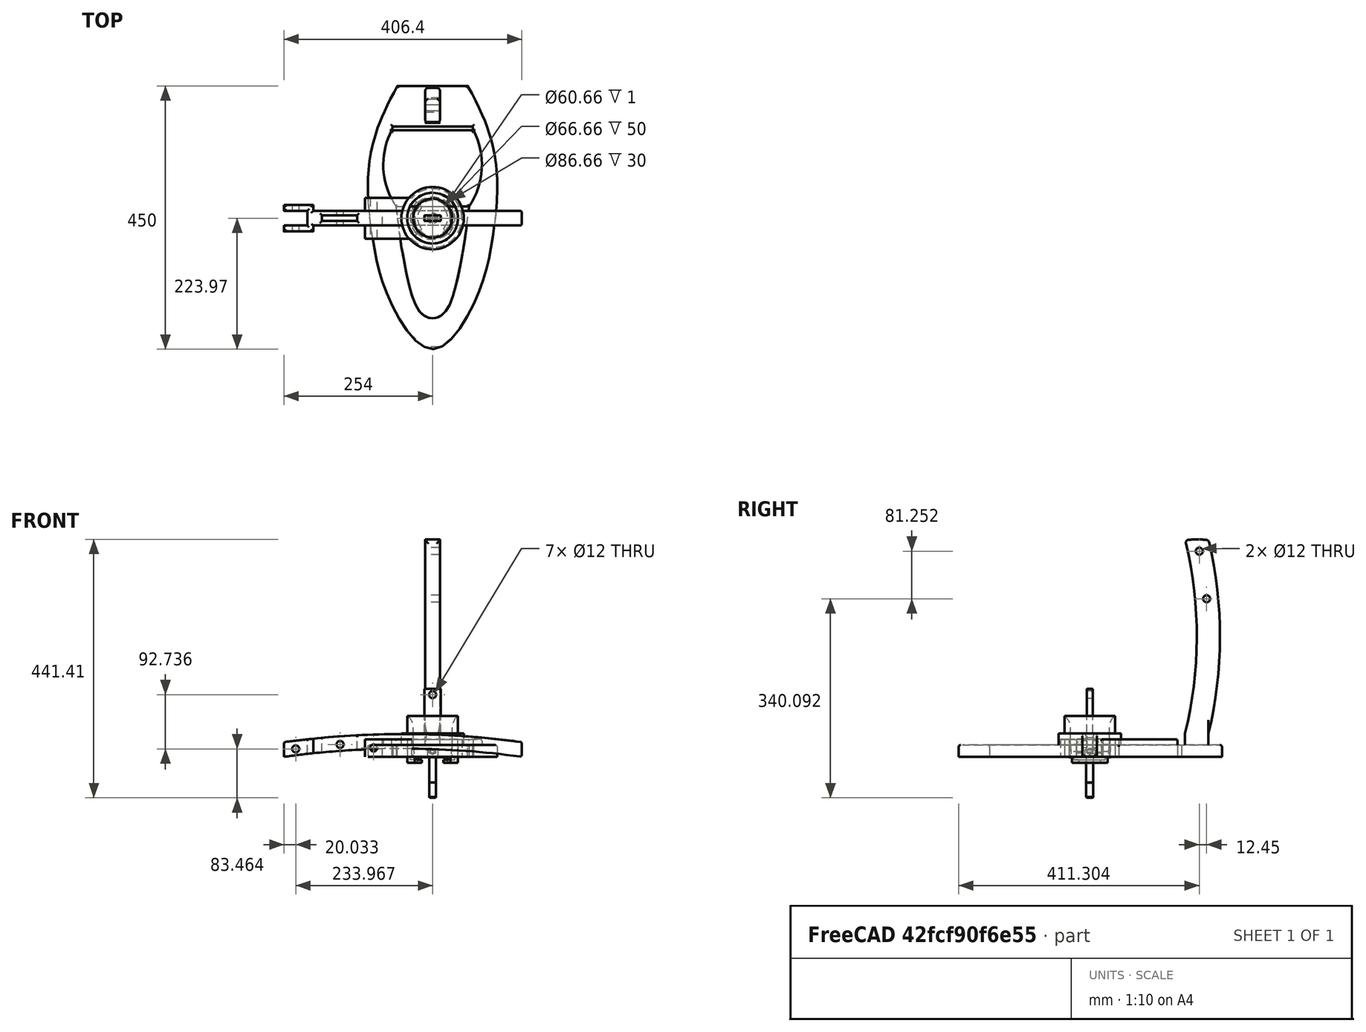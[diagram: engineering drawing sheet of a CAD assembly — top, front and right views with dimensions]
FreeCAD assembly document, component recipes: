
FREECAD ASSEMBLY — COMPONENT RECIPES ("Espresso Machine")

This assembly document has 8 components, labeled P0..P7 below (a component is one placed body or linked part). 5 of them carry a construction recipe — the FreeCAD feature program that regenerates the part from scratch, quoted from this document or its linked companion documents; the rest are supplied as boundary geometry only. No exploded tour is included for this assembly.
COMPONENT P0 — geometry summary ("M12x45-Screw002"; no construction recipe available for this part):
  bounding box: 57.0 x 18.0 x 18.0 mm
  tessellated surface: 6,456 triangles
  volume: 7653 mm^3 (41% of its bounding box)
  symmetry: 6-fold rotationally symmetric about the x axis
COMPONENT P1 — geometry summary ("M6x70-Screw001"; no construction recipe available for this part):
  bounding box: 82.0 x 18.0 x 18.0 mm
  tessellated surface: 6,456 triangles
  volume: 10481 mm^3 (39% of its bounding box)
  symmetry: 6-fold rotationally symmetric about the x axis
COMPONENT P2 — geometry summary ("M6x70-Screw002"; no construction recipe available for this part):
  bounding box: 82.0 x 18.0 x 18.0 mm
  tessellated surface: 6,456 triangles
  volume: 10481 mm^3 (39% of its bounding box)
  symmetry: 6-fold rotationally symmetric about the x axis
COMPONENT P3 — recipe-attached ("Plunger001", modeled in this document).
Construction recipe (the document's own serialized feature program — sketch geometry with constraints, then the solid features built on it; lengths are millimeters unless a unit is written):

FEATURE [Sketcher::SketchObject] Sketch016
  ArcFitTolerance = 1e-06
  AttachmentSupport = -> [YZ_Plane004]
  FullyConstrained = true
  MakeInternals = false
  MapMode = 5
  Placement = pos=(0,0,0) rot=(0.57735,0.57735,0.57735;2.0944rad)
  sketch-geometry (6):
    g0: LineSegment StartX=0 StartY=40 StartZ=0 EndX=33.33 EndY=40 EndZ=0
    g1: LineSegment StartX=33.33 StartY=40 StartZ=0 EndX=33.33 EndY=20 EndZ=0
    g2: LineSegment StartX=31.8 StartY=1.61e-14 StartZ=0 EndX=0 EndY=0 EndZ=0
    g3: ArcOfCircle CenterX=163.284 CenterY=1.61e-14 CenterZ=0 NormalX=0 NormalY=0 NormalZ=1 AngleXU=0 Radius=131.484 StartAngle=2.98889 EndAngle=3.14159
    g4: LineSegment StartX=0 StartY=40 StartZ=0 EndX=0 EndY=0 EndZ=0
    g5: LineSegment [constr] StartX=31.8 StartY=1.61e-14 StartZ=0 EndX=163.284 EndY=1.61e-14 EndZ=0
  constraints (17):
    c: PointOnObject(g0,g-2)
    c: Horizontal(g0)
    c: Coincident(g0,g1)
    c: Vertical(g1)
    c: PointOnObject(g2,g-1)
    c: Coincident(g2,g-1)
    c: Coincident(g3,g1)
    c: Coincident(g3,g2)
    c: DistanceX(g0,g0) = 33.33
    c: Coincident(g4,g0)
    c: Coincident(g4,g2)
    c: DistanceY(g4,g4) = 40
    c: DistanceY(g1,g1) = 20
    c: DistanceX(g2,g2) = 31.8
    c: Coincident(g5,g2)
    c: Coincident(g5,g3)
    c: Horizontal(g5)
FEATURE [PartDesign::Revolution] Revolution004
  Angle = 360
  Angle2 = 60
  Axis = (0,0,1)
  Base = (0,0,0)
  Placement = pos=(0,0,0) rot=(1,1,1;2.0944rad)
  Profile = -> Sketch016
  ReferenceAxis = -> Sketch016 [V_Axis]
  Refine = true
  Reversed = true
  Suppressed = false
  Type = 0
FEATURE [Sketcher::SketchObject] Sketch017
  ArcFitTolerance = 1e-06
  AttachmentSupport = -> [Revolution004]
  FullyConstrained = true
  MakeInternals = false
  MapMode = 5
  Placement = pos=(-8.8e-15,0,40) rot=(0,0,-1;1.5708rad)
  expr: Constraints[8] = VarSet.Plunger_Clearance_Length - 2.5 mm
  sketch-geometry (4):
    g0: LineSegment StartX=-4.995 StartY=13.75 StartZ=0 EndX=-4.995 EndY=-13.75 EndZ=0
    g1: LineSegment StartX=-4.995 StartY=-13.75 StartZ=0 EndX=4.995 EndY=-13.75 EndZ=0
    g2: LineSegment StartX=4.995 StartY=-13.75 StartZ=0 EndX=4.995 EndY=13.75 EndZ=0
    g3: LineSegment StartX=4.995 StartY=13.75 StartZ=0 EndX=-4.995 EndY=13.75 EndZ=0
  constraints (10):
    c: Coincident(g0,g1)
    c: Coincident(g1,g2)
    c: Coincident(g2,g3)
    c: Coincident(g3,g0)
    c: Vertical(g0)
    c: Horizontal(g1)
    c: Symmetric(g0,g2,g-2)
    c: Symmetric(g2,g1,g-1)
    c: DistanceY(g2,g2) = 27.5
    c: Distance(g3,g3) = 9.99
FEATURE [PartDesign::Pad] Pad007
  BaseFeature = -> Revolution004
  Direction = (0,0,1)
  Length = 76.2
  Length2 = 10
  Placement = pos=(0,0,0) rot=(1,1,1;2.0944rad)
  Profile = -> Sketch017
  ReferenceAxis = -> Sketch017 [N_Axis]
  Refine = true
  Suppressed = false
  Type = 0
FEATURE [Sketcher::SketchObject] Sketch018
  ArcFitTolerance = 1e-06
  AttachmentSupport = -> [Pad007]
  ExternalGeometry = -> [Pad007]
  FullyConstrained = true
  MakeInternals = false
  MapMode = 5
  Placement = pos=(0,-4.995,0) rot=(0.57735,0.57735,-0.57735;2.0944rad)
  sketch-geometry (1):
    g0: Circle CenterX=-106.2 CenterY=0 CenterZ=0 NormalX=0 NormalY=0 NormalZ=1 AngleXU=0 Radius=6
  constraints (3):
    c: PointOnObject(g0,g-1)
    c: Diameter(g0) = 12
    c: Distance(g0,g-3) = 10
FEATURE [PartDesign::Pocket] Pocket005
  BaseFeature = -> Pad007
  Direction = (0,1,0)
  Length = 5
  Length2 = 5
  Placement = pos=(0,0,0) rot=(1,1,1;2.0944rad)
  Profile = -> Sketch018
  ReferenceAxis = -> Sketch018 [N_Axis]
  Refine = true
  Suppressed = false
  Type = 1
FEATURE [PartDesign::Fillet] Fillet003
  Base = -> Pocket005 [Face8,Edge15,Edge8,Edge10,Edge12]
  BaseFeature = -> Pocket005
  Placement = pos=(0,0,0) rot=(1,1,1;2.0944rad)
  Radius = 1
  Refine = true
  SupportTransform = false
  Suppressed = false
  UseAllEdges = false
FEATURE [PartDesign::Fillet] Fillet004
  Base = -> Fillet003 [Edge28,Edge47]
  BaseFeature = -> Fillet003
  Placement = pos=(0,0,0) rot=(1,1,1;2.0944rad)
  Radius = 1
  Refine = true
  SupportTransform = false
  Suppressed = false
  UseAllEdges = false
FEATURE [PartDesign::Body] Body004  label="Plunger"
  AllowCompound = false
  Group = -> [Sketch016,Revolution004,Sketch017,Pad007,Sketch018,Pocket005,Fillet003,Fillet004]
  Origin = -> Origin004
  Tip = -> Fillet004
COMPONENT P4 — recipe-attached ("Pressure Vessel001", modeled in this document).
Construction recipe (the document's own serialized feature program — sketch geometry with constraints, then the solid features built on it; lengths are millimeters unless a unit is written):

FEATURE [Sketcher::SketchObject] Sketch
  ArcFitTolerance = 1e-06
  AttachmentSupport = -> [XY_Plane]
  FullyConstrained = true
  MakeInternals = false
  MapMode = 5
  sketch-geometry (2):
    g0: Circle CenterX=0 CenterY=0 CenterZ=0 NormalX=0 NormalY=0 NormalZ=1 AngleXU=0 Radius=33.33
    g1: Circle CenterX=0 CenterY=0 CenterZ=0 NormalX=0 NormalY=0 NormalZ=1 AngleXU=0 Radius=43.33
  constraints (4):
    c: Coincident(g0,g-1)
    c: Coincident(g1,g0)
    c: Diameter(g0) = 66.66
    c: Diameter(g1) = 86.66
FEATURE [PartDesign::Pad] Pad
  Direction = (0,0,1)
  Length = 50
  Length2 = 10
  Profile = -> Sketch
  ReferenceAxis = -> Sketch [N_Axis]
  Refine = true
  Suppressed = false
  Type = 0
FEATURE [Sketcher::SketchObject] Sketch001
  ArcFitTolerance = 1e-06
  AttachmentSupport = -> [XZ_Plane]
  ExternalGeometry = -> [Pad]
  FullyConstrained = true
  MakeInternals = false
  MapMode = 5
  Placement = pos=(0,0,0) rot=(1,0,0;1.5708rad)
  sketch-geometry (4):
    g0: LineSegment StartX=33.33 StartY=50 StartZ=0 EndX=43.33 EndY=50 EndZ=0
    g1: LineSegment StartX=43.33 StartY=50 StartZ=0 EndX=43.33 EndY=70 EndZ=0
    g2: ArcOfCircle CenterX=58.33 CenterY=50 CenterZ=0 NormalX=0 NormalY=0 NormalZ=1 AngleXU=0 Radius=25 StartAngle=2.2143 EndAngle=3.14159
    g3: LineSegment [constr] StartX=33.33 StartY=50 StartZ=0 EndX=33.33 EndY=0 EndZ=0
  constraints (11):
    c: Coincident(g0,g-4)
    c: Coincident(g0,g-3)
    c: Coincident(g0,g1)
    c: Vertical(g1)
    c: DistanceY(g1,g1) = 20
    c: Coincident(g2,g0)
    c: Coincident(g2,g1)
    c: Coincident(g3,g0)
    c: PointOnObject(g3,g-1)
    c: Vertical(g3)
    c: Tangent(g3,g2)
FEATURE [PartDesign::Revolution] Revolution
  Angle = 360
  Angle2 = 60
  Axis = (0,2e-16,1)
  Base = (0,0,0)
  BaseFeature = -> Pad
  Profile = -> Sketch001
  ReferenceAxis = -> Sketch001 [V_Axis]
  Refine = true
  Suppressed = false
  Type = 0
FEATURE [Sketcher::SketchObject] Sketch002
  ArcFitTolerance = 1e-06
  AttachmentSupport = -> [XZ_Plane]
  ExternalGeometry = -> [Revolution]
  FullyConstrained = true
  MakeInternals = false
  MapMode = 5
  Placement = pos=(0,0,0) rot=(1,0,0;1.5708rad)
  sketch-geometry (8):
    g0: LineSegment StartX=43.33 StartY=0 StartZ=0 EndX=43.33 EndY=-10 EndZ=0
    g1: LineSegment StartX=43.33 StartY=-10 StartZ=0 EndX=25.83 EndY=-10 EndZ=0
    g2: LineSegment StartX=25.83 StartY=-10 StartZ=0 EndX=25.83 EndY=-5 EndZ=0
    g3: LineSegment StartX=25.83 StartY=-5 StartZ=0 EndX=38.33 EndY=-5 EndZ=0
    g4: LineSegment StartX=38.33 StartY=-5 StartZ=0 EndX=38.33 EndY=0 EndZ=0
    g5: LineSegment [constr] StartX=43.33 StartY=0 StartZ=0 EndX=38.33 EndY=0 EndZ=0
    g6: LineSegment [constr] StartX=38.33 StartY=0 StartZ=0 EndX=33.33 EndY=0 EndZ=0
    g7: LineSegment StartX=38.33 StartY=0 StartZ=0 EndX=43.33 EndY=0 EndZ=0
  constraints (21):
    c: Coincident(g0,g-3)
    c: Vertical(g0)
    c: Coincident(g0,g1)
    c: Horizontal(g1)
    c: Coincident(g1,g2)
    c: Vertical(g2)
    c: Coincident(g2,g3)
    c: Coincident(g4,g3)
    c: PointOnObject(g4,g-1)
    c: Vertical(g4)
    c: Horizontal(g3)
    c: DistanceX(g1,g1) = 17.5
    c: DistanceY(g0,g0) = 10
    c: Equal(g2,g4)
    c: Coincident(g5,g0)
    c: Coincident(g5,g4)
    c: Coincident(g6,g4)
    c: Coincident(g6,g-4)
    c: Equal(g6,g5)
    c: Coincident(g7,g4)
    c: Coincident(g7,g0)
FEATURE [PartDesign::Revolution] Revolution001
  Angle = 90
  Angle2 = 60
  Axis = (0,2e-16,1)
  Base = (0,0,0)
  BaseFeature = -> Revolution
  Midplane = true
  Profile = -> Sketch002
  ReferenceAxis = -> Sketch002 [V_Axis]
  Refine = true
  Suppressed = false
  Type = 0
FEATURE [PartDesign::Mirrored] Mirrored
  BaseFeature = -> Revolution001
  MirrorPlane = -> Sketch002 [V_Axis]
  Originals = -> [Revolution001]
  Refine = true
  Suppressed = false
  TransformMode = 0
FEATURE [Sketcher::SketchObject] Sketch003
  ArcFitTolerance = 1e-06
  AttachmentSupport = -> [XZ_Plane]
  ExternalGeometry = -> [Mirrored]
  FullyConstrained = true
  MakeInternals = false
  MapMode = 5
  Placement = pos=(0,0,0) rot=(1,0,0;1.5708rad)
  sketch-geometry (5):
    g0: LineSegment StartX=36.33 StartY=0 StartZ=0 EndX=33.33 EndY=0 EndZ=0
    g1: LineSegment StartX=33.33 StartY=0 StartZ=0 EndX=30.33 EndY=0 EndZ=0
    g2: LineSegment StartX=30.33 StartY=0 StartZ=0 EndX=30.33 EndY=-1 EndZ=0
    g3: LineSegment StartX=30.33 StartY=-1 StartZ=0 EndX=36.33 EndY=-1 EndZ=0
    g4: LineSegment StartX=36.33 StartY=-1 StartZ=0 EndX=36.33 EndY=0 EndZ=0
  constraints (14):
    c: PointOnObject(g0,g-1)
    c: Coincident(g0,g-3)
    c: Coincident(g0,g1)
    c: Horizontal(g1)
    c: Coincident(g1,g2)
    c: Vertical(g2)
    c: Coincident(g2,g3)
    c: Horizontal(g3)
    c: Coincident(g3,g4)
    c: Coincident(g4,g0)
    c: Vertical(g4)
    c: Equal(g1,g0)
    c: DistanceX(g3,g3) = 6
    c: DistanceY(g4,g4) = 1
FEATURE [PartDesign::Revolution] Revolution002
  Angle = 360
  Angle2 = 60
  Axis = (0,2e-16,1)
  Base = (0,0,0)
  BaseFeature = -> Mirrored
  Midplane = true
  Profile = -> Sketch003
  ReferenceAxis = -> Sketch003 [V_Axis]
  Refine = true
  Suppressed = false
  Type = 0
FEATURE [Sketcher::SketchObject] Sketch004
  ArcFitTolerance = 1e-06
  AttachmentSupport = -> [XZ_Plane]
  ExternalGeometry = -> [Revolution002]
  FullyConstrained = true
  MakeInternals = false
  MapMode = 5
  Placement = pos=(0,0,0) rot=(1,0,0;1.5708rad)
  sketch-geometry (4):
    g0: LineSegment StartX=33.33 StartY=20 StartZ=0 EndX=53.33 EndY=20 EndZ=0
    g1: LineSegment StartX=53.33 StartY=20 StartZ=0 EndX=53.33 EndY=40 EndZ=0
    g2: LineSegment StartX=53.33 StartY=40 StartZ=0 EndX=33.33 EndY=40 EndZ=0
    g3: LineSegment StartX=33.33 StartY=40 StartZ=0 EndX=33.33 EndY=20 EndZ=0
  constraints (12):
    c: Horizontal(g0)
    c: Horizontal(g2)
    c: Vertical(g1)
    c: Vertical(g3)
    c: DistanceX(g2,g2) = 20
    c: DistanceY(g1,g1) = 20
    c: Coincident(g1,g0)
    c: Coincident(g2,g1)
    c: Coincident(g3,g2)
    c: Coincident(g3,g0)
    c: PointOnObject(g0,g-3)
    c: DistanceY(g-1,g0) = 20
FEATURE [PartDesign::Revolution] Revolution003
  Angle = 360
  Angle2 = 60
  Axis = (0,2e-16,1)
  Base = (0,0,0)
  BaseFeature = -> Revolution002
  Profile = -> Sketch004
  ReferenceAxis = -> Sketch004 [V_Axis]
  Refine = true
  Suppressed = false
  Type = 0
FEATURE [PartDesign::Body] Body  label="Pressure Vessel"
  AllowCompound = false
  Group = -> [Sketch,Pad,Sketch001,Revolution,Sketch002,Revolution001,Mirrored,Sketch003,Revolution002,Sketch004,Revolution003]
  Origin = -> Origin
  Tip = -> Revolution003
COMPONENT P5 — recipe-attached ("Presure Lever001", modeled in this document).
Construction recipe (the document's own serialized feature program — sketch geometry with constraints, then the solid features built on it; lengths are millimeters unless a unit is written):

FEATURE [Sketcher::SketchObject] Sketch011
  ArcFitTolerance = 1e-06
  AttachmentSupport = -> [XY_Plane002]
  FullyConstrained = true
  MakeInternals = false
  MapMode = 5
  expr: Constraints[43] = VarSet.Plunger_Clearance_Length * 2
  expr: Constraints[45] = VarSet.Plunger_Clearance_Length / 2
  sketch-geometry (16):
    g0: LineSegment StartX=-214 StartY=-12.5 StartZ=0 EndX=-214 EndY=12.5 EndZ=0
    g1: LineSegment StartX=-214 StartY=12.5 StartZ=0 EndX=-254 EndY=12.5 EndZ=0
    g2: LineSegment StartX=-254 StartY=12.5 StartZ=0 EndX=-254 EndY=22.5 EndZ=0
    g3: LineSegment StartX=152.4 StartY=12.5 StartZ=0 EndX=152.4 EndY=-12.5 EndZ=0
    g4: LineSegment StartX=-254 StartY=-22.5 StartZ=0 EndX=-254 EndY=-12.5 EndZ=0
    g5: LineSegment StartX=-254 StartY=-12.5 StartZ=0 EndX=-214 EndY=-12.5 EndZ=0
    g6: LineSegment StartX=-254 StartY=22.5 StartZ=0 EndX=-204 EndY=22.5 EndZ=0
    g7: LineSegment StartX=-204 StartY=22.5 StartZ=0 EndX=-204 EndY=12.5 EndZ=0
    g8: LineSegment StartX=-204 StartY=12.5 StartZ=0 EndX=152.4 EndY=12.5 EndZ=0
    g9: LineSegment StartX=-254 StartY=-22.5 StartZ=0 EndX=-204 EndY=-22.5 EndZ=0
    g10: LineSegment StartX=-204 StartY=-22.5 StartZ=0 EndX=-204 EndY=-12.5 EndZ=0
    g11: LineSegment StartX=-204 StartY=-12.5 StartZ=0 EndX=152.4 EndY=-12.5 EndZ=0
    g12: LineSegment StartX=-189 StartY=5 StartZ=0 EndX=-189 EndY=-5 EndZ=0
    g13: LineSegment StartX=-189 StartY=-5 StartZ=0 EndX=-129 EndY=-5 EndZ=0
    g14: LineSegment StartX=-129 StartY=-5 StartZ=0 EndX=-129 EndY=5 EndZ=0
    g15: LineSegment StartX=-129 StartY=5 StartZ=0 EndX=-189 EndY=5 EndZ=0
  constraints (46):
    c: Coincident(g0,g1)
    c: Horizontal(g1)
    c: Coincident(g1,g2)
    c: Vertical(g2)
    c: Vertical(g4)
    c: Coincident(g4,g5)
    c: Coincident(g5,g0)
    c: Horizontal(g5)
    c: Equal(g2,g4)
    c: Symmetric(g3,g3,g-1)
    c: DistanceY(g0,g0) = 25
    c: DistanceX(g1,g1) = 40
    c: Equal(g1,g5)
    c: Symmetric(g0,g0,g-1)
    c: DistanceY(g2,g2) = 10
    c: Coincident(g2,g6)
    c: Horizontal(g6)
    c: Coincident(g6,g7)
    c: Vertical(g7)
    c: Coincident(g7,g8)
    c: Horizontal(g8)
    c: Coincident(g4,g9)
    c: Horizontal(g9)
    c: Coincident(g9,g10)
    c: Vertical(g10)
    c: Coincident(g10,g11)
    c: Horizontal(g11)
    c: Vertical(g11,g8)
    c: Vertical(g7,g10)
    c: Equal(g7,g10)
    c: Horizontal(g0,g7)
    c: DistanceX(g0,g7) = 10
    c: DistanceX(g2,g3) = 406.4
    c: Coincident(g8,g3)
    c: Distance(g3,g-2) = 152.4
    c: Coincident(g12,g13)
    c: Coincident(g13,g14)
    c: Coincident(g14,g15)
    c: Coincident(g15,g12)
    c: Vertical(g12)
    c: Horizontal(g13)
    c: Horizontal(g15)
    c: Symmetric(g14,g13,g-1)
    c: DistanceX(g15,g15) = 60
    c: Distance(g14,g14) = 10
    c: DistanceX(g7,g12) = 15
FEATURE [PartDesign::Pad] Pad005
  Direction = (0,0,1)
  Length = 40
  Length2 = 10
  Profile = -> Sketch011
  ReferenceAxis = -> Sketch011 [N_Axis]
  Refine = true
  Suppressed = false
  Type = 0
FEATURE [Sketcher::SketchObject] Sketch012
  ArcFitTolerance = 1e-06
  AttachmentSupport = -> [Pad005]
  ExternalGeometry = -> [Pad005]
  FullyConstrained = true
  MakeInternals = false
  MapMode = 5
  Placement = pos=(0,-12.5,0) rot=(1,0,0;1.5708rad)
  sketch-geometry (6):
    g0: ArcOfCircle CenterX=-50.8 CenterY=-1468.03 CenterZ=0 NormalX=0 NormalY=0 NormalZ=1 AngleXU=0 Radius=1482.03 StartAngle=1.43325 EndAngle=1.70834
    g1: ArcOfCircle CenterX=-50.8 CenterY=-1468.03 CenterZ=0 NormalX=0 NormalY=0 NormalZ=1 AngleXU=0 Radius=1506.8 StartAngle=1.43553 EndAngle=1.70606
    g2: LineSegment StartX=-254 StartY=2.274e-13 StartZ=0 EndX=152.4 EndY=-2.274e-13 EndZ=0
    g3: LineSegment StartX=-254 StartY=25 StartZ=0 EndX=-254 EndY=40 EndZ=0
    g4: LineSegment StartX=152.4 StartY=40 StartZ=0 EndX=152.4 EndY=25 EndZ=0
    g5: LineSegment StartX=-254 StartY=40 StartZ=0 EndX=152.4 EndY=40 EndZ=0
  constraints (15):
    c: Coincident(g0,g-5)
    c: Coincident(g0,g-6)
    c: PointOnObject(g1,g-5)
    c: PointOnObject(g1,g-6)
    c: Coincident(g1,g0)
    c: DistanceY(g0,g1) = 25
    c: Coincident(g2,g0)
    c: Coincident(g2,g0)
    c: Coincident(g3,g1)
    c: Coincident(g3,g-9)
    c: Coincident(g4,g-8)
    c: Coincident(g4,g1)
    c: Coincident(g5,g3)
    c: Coincident(g5,g4)
    c: Radius(g0) = 1482.03
FEATURE [PartDesign::Pocket] Pocket002
  BaseFeature = -> Pad005
  Direction = (0,1,-2e-16)
  Length = 5
  Length2 = 5
  Midplane = true
  Profile = -> Sketch012
  ReferenceAxis = -> Sketch012 [N_Axis]
  Refine = true
  Suppressed = false
  Type = 1
FEATURE [PartDesign::Fillet] Fillet002
  Base = -> Pocket002 [Face14,Face4]
  BaseFeature = -> Pocket002
  Radius = 3
  Refine = true
  SupportTransform = false
  Suppressed = false
  UseAllEdges = false
FEATURE [Sketcher::SketchObject] Sketch013
  ArcFitTolerance = 1e-06
  AttachmentSupport = -> [Fillet002]
  ExternalGeometry = -> [Fillet002]
  FullyConstrained = true
  MakeInternals = false
  MapMode = 5
  Placement = pos=(0,-12.5,0) rot=(1,0,0;1.5708rad)
  sketch-geometry (6):
    g0: Circle CenterX=-158.2 CenterY=21.0121 CenterZ=0 NormalX=0 NormalY=0 NormalZ=1 AngleXU=0 Radius=6
    g1: Circle CenterX=-233.967 CenterY=13.4636 CenterZ=0 NormalX=0 NormalY=0 NormalZ=1 AngleXU=0 Radius=6
    g2: LineSegment [constr] StartX=-159.034 StartY=31.8641 StartZ=0 EndX=-158.2 EndY=21.0121 EndZ=0
    g3: LineSegment [constr] StartX=-158.2 StartY=21.0121 StartZ=0 EndX=-157.366 EndY=10.1601 EndZ=0
    g4: LineSegment [constr] StartX=-254 StartY=21.9723 StartZ=0 EndX=-214 EndY=4.98325 EndZ=0
    g5: LineSegment [constr] StartX=-214 StartY=26.8823 StartZ=0 EndX=-254 EndY=2.238e-13 EndZ=0
  constraints (15):
    c: Diameter(g0) = 12
    c: Diameter(g1) = 12
    c: Symmetric(g-9,g-8,g2)
    c: Coincident(g0,g2)
    c: Coincident(g0,g3)
    c: Parallel(g3,g2)
    c: Equal(g2,g3)
    c: Coincident(g4,g-4)
    c: Coincident(g4,g-11)
    c: Coincident(g5,g-5)
    c: Coincident(g5,g-11)
    c: PointOnObject(g1,g4)
    c: PointOnObject(g1,g5)
    c: PointOnObject(g2,g-8)
    c: PointOnObject(g3,g-7)
FEATURE [PartDesign::Pocket] Pocket003
  BaseFeature = -> Fillet002
  Direction = (0,1,-2e-16)
  Length = 5
  Length2 = 5
  Midplane = true
  Profile = -> Sketch013
  ReferenceAxis = -> Sketch013 [N_Axis]
  Refine = true
  Suppressed = false
  Type = 1
FEATURE [PartDesign::Body] Body002  label="Presure Lever"
  AllowCompound = false
  Group = -> [Sketch011,Pad005,Sketch012,Pocket002,Fillet002,Sketch013,Pocket003]
  Origin = -> Origin002
  Tip = -> Pocket003
COMPONENT P6 — recipe-attached ("Stand001", modeled in this document).
Construction recipe (the document's own serialized feature program — sketch geometry with constraints, then the solid features built on it; lengths are millimeters unless a unit is written):

FEATURE [Sketcher::SketchObject] Sketch005
  ArcFitTolerance = 1e-06
  AttachmentSupport = -> [XY_Plane001]
  FullyConstrained = true
  MakeInternals = false
  MapMode = 5
  sketch-geometry (22):
    g0: LineSegment StartX=-60 StartY=226.026 StartZ=0 EndX=60 EndY=226.026 EndZ=0
    g1-g11: Circle [constr] x11 (B-spline internal-alignment scaffolding for g12; pole/knot coordinates omitted)
    g12: BSplineCurve PolesCount=11 KnotsCount=9 Degree=3 IsPeriodic=0
    g13-g21: GeomPoint [constr] x9 (B-spline internal-alignment scaffolding for g12; pole/knot coordinates omitted)
  constraints (15):
    c: Weight(g1) = 1
    c: Equal(g1, g2-g11) x10
    c: InternalAlignment(g1-g11 -> g12) x11
    c: InternalAlignment(g13-g21 -> g12) x9
    c: Coincident(g1,g0)
    c: PointOnObject(g6,g-2)
    c: Coincident(g11,g0)
    c: Symmetric(g19,g15,g-2)
    c: Symmetric(g18,g16,g-2)
    c: Symmetric(g20,g14,g-2)
    c: Symmetric(g10,g2,g-2)
    c: Distance(g17,g0) = 450
    c: Symmetric(g12,g12,g-2)
    c: DistanceX(g0,g0) = 120
    c: Block(g12)
FEATURE [PartDesign::Pad] Pad001
  Direction = (0,0,1)
  Length = 20
  Length2 = 10
  Profile = -> Sketch005
  ReferenceAxis = -> Sketch005 [N_Axis]
  Refine = true
  Suppressed = false
  Type = 0
FEATURE [Sketcher::SketchObject] Sketch006
  ArcFitTolerance = 1e-06
  AttachmentSupport = -> [Pad001]
  ExternalGeometry = -> [Pad001]
  FullyConstrained = true
  MakeInternals = false
  MapMode = 5
  Placement = pos=(0,0,20) rot=(0,0,1;0rad)
  sketch-geometry (8):
    g0: LineSegment StartX=-70 StartY=150 StartZ=0 EndX=70 EndY=150 EndZ=0
    g1: LineSegment StartX=-62.5 StartY=20 StartZ=0 EndX=62.5 EndY=20 EndZ=0
    g2: ArcOfCircle CenterX=42.9677 CenterY=91.301 CenterZ=0 NormalX=0 NormalY=0 NormalZ=1 AngleXU=0 Radius=127.308 StartAngle=2.66238 EndAngle=3.73606
    g3: LineSegment [constr] StartX=-109.336 StartY=82.5143 StartZ=0 EndX=-84.1287 EndY=83.9685 EndZ=0
    g4: ArcOfCircle CenterX=-42.9677 CenterY=91.301 CenterZ=0 NormalX=0 NormalY=0 NormalZ=1 AngleXU=0 Radius=127.308 StartAngle=5.68872 EndAngle=6.7624
    g5: LineSegment [constr] StartX=84.1287 StartY=83.9685 StartZ=0 EndX=109.336 EndY=82.5143 EndZ=0
    g6: LineSegment [constr] StartX=70 StartY=150 StartZ=0 EndX=95.2493 EndY=150 EndZ=0
    g7: LineSegment [constr] StartX=-70 StartY=150 StartZ=0 EndX=-95.2493 EndY=150 EndZ=0
  constraints (24):
    c: Symmetric(g0,g0,g-2)
    c: Symmetric(g1,g1,g-2)
    c: DistanceX(g0,g0) = 140
    c: DistanceX(g1,g1) = 125
    c: Distance(g-1,g0) = 150
    c: Coincident(g2,g0)
    c: Coincident(g2,g1)
    c: PointOnObject(g3,g-4)
    c: PointOnObject(g3,g2)
    c: Coincident(g4,g0)
    c: Coincident(g4,g1)
    c: PointOnObject(g5,g4)
    c: PointOnObject(g5,g-4)
    c: Symmetric(g0,g1,g5)
    c: Symmetric(g0,g1,g3)
    c: Equal(g3,g5)
    c: Coincident(g6,g0)
    c: PointOnObject(g6,g-4)
    c: Parallel(g6,g0)
    c: Equal(g6,g5)
    c: Coincident(g7,g0)
    c: PointOnObject(g7,g-4)
    c: Horizontal(g7)
    c: Distance(g-1,g1) = 20
FEATURE [PartDesign::Pad] Pad002
  BaseFeature = -> Pad001
  Direction = (0,0,1)
  Length = 10
  Length2 = 10
  Profile = -> Sketch006
  ReferenceAxis = -> Sketch006 [N_Axis]
  Refine = true
  Suppressed = false
  Type = 0
FEATURE [Sketcher::SketchObject] Sketch007
  ArcFitTolerance = 1e-06
  AttachmentSupport = -> [Pad002]
  ExternalGeometry = -> [Pad002]
  FullyConstrained = true
  MakeInternals = false
  MapMode = 5
  Placement = pos=(0,0,20) rot=(0,0,1;0rad)
  sketch-geometry (37):
    g0-g8: Circle [constr] x9 (B-spline internal-alignment scaffolding for g9; pole/knot coordinates omitted)
    g9: BSplineCurve PolesCount=9 KnotsCount=7 Degree=3 IsPeriodic=0
    g10-g16: GeomPoint [constr] x7 (B-spline internal-alignment scaffolding for g9; pole/knot coordinates omitted)
    g17: LineSegment [constr] StartX=-62.5 StartY=20 StartZ=0 EndX=-109.196 EndY=20 EndZ=0
    g18: LineSegment [constr] StartX=62.5 StartY=20 StartZ=0 EndX=109.196 EndY=20 EndZ=0
    g19: LineSegment [constr] StartX=54.2197 StartY=-43.9087 StartZ=0 EndX=100.915 EndY=-43.9087 EndZ=0
    g20: LineSegment [constr] StartX=-54.2197 StartY=-43.9087 StartZ=0 EndX=-100.915 EndY=-43.9087 EndZ=0
    g21: LineSegment [constr] StartX=49.9941 StartY=-66.9467 StartZ=0 EndX=96.6898 EndY=-66.9467 EndZ=0
    g22: LineSegment [constr] StartX=-49.9941 StartY=-66.9467 StartZ=0 EndX=-96.6898 EndY=-66.9467 EndZ=0
    g23: LineSegment [constr] StartX=-33.1368 StartY=-158.556 StartZ=0 EndX=-33.1368 EndY=-205.252 EndZ=0
    g24: LineSegment [constr] StartX=33.1368 StartY=-158.556 StartZ=0 EndX=33.1368 EndY=-205.252 EndZ=0
    g25: LineSegment [constr] StartX=0 StartY=-177.278 StartZ=0 EndX=0 EndY=-223.974 EndZ=0
    g26: LineSegment StartX=-62.5 StartY=20 StartZ=0 EndX=62.5 EndY=20 EndZ=0
    g27: LineSegment StartX=-70 StartY=150 StartZ=0 EndX=70 EndY=150 EndZ=0
    g28: LineSegment StartX=-70 StartY=150 StartZ=0 EndX=-68.2 EndY=156.718 EndZ=0
    g29: LineSegment StartX=70 StartY=150 StartZ=0 EndX=68.2 EndY=156.718 EndZ=0
    g30: LineSegment StartX=-68.2 StartY=156.718 StartZ=0 EndX=68.2 EndY=156.718 EndZ=0
    g31: LineSegment [constr] StartX=-109.196 StartY=20 StartZ=0 EndX=-100.915 EndY=-43.9087 EndZ=0
    g32: LineSegment [constr] StartX=-100.915 StartY=-43.9087 StartZ=0 EndX=-96.6898 EndY=-66.9467 EndZ=0
    g33: LineSegment [constr] StartX=109.196 StartY=20 StartZ=0 EndX=100.915 EndY=-43.9087 EndZ=0
    g34: LineSegment [constr] StartX=100.915 StartY=-43.9087 StartZ=0 EndX=96.6898 EndY=-66.9467 EndZ=0
    g35: LineSegment [constr] StartX=33.1368 StartY=-205.252 StartZ=0 EndX=0 EndY=-223.974 EndZ=0
    g36: LineSegment [constr] StartX=-33.1368 StartY=-205.252 StartZ=0 EndX=0 EndY=-223.974 EndZ=0
  constraints (66):
    c: Weight(g0) = 1
    c: Equal(g0, g1-g8) x8
    c: InternalAlignment(g0-g8 -> g9) x9
    c: InternalAlignment(g10-g16 -> g9) x7
    c: Coincident(g0,g-5)
    c: PointOnObject(g4,g-2)
    c: Coincident(g8,g-4)
    c: Symmetric(g11,g15,g-2)
    c: Symmetric(g12,g14,g-2)
    c: Symmetric(g7,g1,g-2)
    c: Coincident(g17,g9)
    c: PointOnObject(g17,g-6)
    c: Horizontal(g17)
    c: Coincident(g18,g9)
    c: PointOnObject(g18,g-6)
    c: Coincident(g19,g7)
    c: PointOnObject(g19,g-6)
    c: Coincident(g20,g1)
    c: PointOnObject(g20,g-6)
    c: Coincident(g21,g15)
    c: PointOnObject(g21,g-6)
    c: Coincident(g22,g11)
    c: PointOnObject(g22,g-6)
    c: Coincident(g23,g3)
    c: PointOnObject(g23,g-6)
    c: Coincident(g24,g5)
    c: PointOnObject(g24,g-6)
    c: Coincident(g25,g4)
    c: PointOnObject(g25,g-6)
    c: Vertical(g25)
    c: Equal(g23,g22)
    c: Equal(g22,g20)
    c: Equal(g20,g17)
    c: Equal(g18,g19)
    c: Equal(g19,g21)
    c: Equal(g21,g24)
    c: Equal(g23,g25)
    c: Equal(g24,g25)
    c: Parallel(g24,g23)
    c: Parallel(g22,g21)
    c: Coincident(g27,g-7)
    c: Coincident(g27,g-7)
    c: Coincident(g28,g27)
    c: Coincident(g29,g27)
    c: Coincident(g30,g28)
    c: Coincident(g30,g29)
    c: Horizontal(g30)
    c: Angle(g29,g27) = 1.309
    c: Angle(g27,g28) = 1.309
    c: Coincident(g26,g0)
    c: Coincident(g26,g8)
    c: Parallel(g19,g21)
    c: Coincident(g31,g17)
    c: Coincident(g31,g20)
    c: Coincident(g32,g20)
    c: Coincident(g32,g22)
    c: Coincident(g33,g18)
    c: Coincident(g33,g19)
    c: Coincident(g34,g19)
    c: Coincident(g34,g21)
    c: Coincident(g35,g24)
    c: Coincident(g35,g25)
    c: Coincident(g36,g23)
    c: Coincident(g36,g25)
    c: Block(g9)
    c: DistanceX(g30,g30) = 136.4
FEATURE [PartDesign::Pocket] Pocket
  BaseFeature = -> Pad002
  Direction = (0,0,-1)
  Length = 5
  Length2 = 5
  Profile = -> Sketch007
  ReferenceAxis = -> Sketch007 [N_Axis]
  Refine = true
  Suppressed = false
  Type = 1
FEATURE [PartDesign::Fillet] Fillet
  Base = -> Pocket [Edge30,Edge27,Edge6,Edge4,Edge14,Edge16,Edge18,Edge31,Edge32,Edge17]
  BaseFeature = -> Pocket
  Radius = 3
  Refine = true
  SupportTransform = false
  Suppressed = false
  UseAllEdges = false
FEATURE [Sketcher::SketchObject] Sketch008
  ArcFitTolerance = 1e-06
  AttachmentSupport = -> [Fillet]
  ExternalGeometry = -> [Fillet]
  FullyConstrained = true
  MakeInternals = false
  MapMode = 5
  Placement = pos=(0,0,20) rot=(0,0,1;0rad)
  sketch-geometry (4):
    g0: LineSegment StartX=-12.5 StartY=203.026 StartZ=0 EndX=-12.5 EndY=163.026 EndZ=0
    g1: LineSegment StartX=-12.5 StartY=163.026 StartZ=0 EndX=12.5 EndY=163.026 EndZ=0
    g2: LineSegment StartX=12.5 StartY=163.026 StartZ=0 EndX=12.5 EndY=203.026 EndZ=0
    g3: LineSegment StartX=12.5 StartY=203.026 StartZ=0 EndX=-12.5 EndY=203.026 EndZ=0
  constraints (11):
    c: Coincident(g0,g1)
    c: Coincident(g1,g2)
    c: Coincident(g2,g3)
    c: Coincident(g3,g0)
    c: Vertical(g0)
    c: Vertical(g2)
    c: Horizontal(g3)
    c: Symmetric(g1,g0,g-2)
    c: Distance(g-3,g3) = 20
    c: DistanceX(g3,g3) = 25
    c: DistanceY(g2,g2) = 40
FEATURE [PartDesign::Pad] Pad003
  BaseFeature = -> Fillet
  Direction = (0,0,1)
  Length = 20
  Length2 = 10
  Profile = -> Sketch008
  ReferenceAxis = -> Sketch008 [N_Axis]
  Refine = true
  Suppressed = false
  Type = 0
FEATURE [Sketcher::SketchObject] Sketch009
  ArcFitTolerance = 1e-06
  AttachmentSupport = -> [YZ_Plane001]
  ExternalGeometry = -> [Pad003]
  FullyConstrained = true
  MakeInternals = false
  MapMode = 5
  Placement = pos=(0,0,0) rot=(0.57735,0.57735,0.57735;2.0944rad)
  sketch-geometry (5):
    g0: ArcOfCircle CenterX=-483.424 CenterY=205.1 CenterZ=0 NormalX=0 NormalY=0 NormalZ=1 AngleXU=0 Radius=706.025 StartAngle=6.04716 EndAngle=6.51922
    g1: ArcOfCircle CenterX=-508.424 CenterY=205.1 CenterZ=0 NormalX=0 NormalY=0 NormalZ=1 AngleXU=0 Radius=691.45 StartAngle=6.04208 EndAngle=6.52429
    g2: LineSegment [constr] StartX=183.026 StartY=205.1 StartZ=0 EndX=222.602 EndY=205.1 EndZ=0
    g3: LineSegment StartX=163.026 StartY=40 StartZ=0 EndX=203.026 EndY=40 EndZ=0
    g4: ArcOfCircle CenterX=183.026 CenterY=205.1 CenterZ=0 NormalX=0 NormalY=0 NormalZ=1 AngleXU=0 Radius=166.307 StartAngle=1.45025 EndAngle=1.69135
  constraints (15):
    c: Coincident(g0,g-3)
    c: Coincident(g1,g-3)
    c: Horizontal(g0,g1)
    c: DistanceX(g1,g0) = 25
    c: DistanceY(g0,g0) = 330.2
    c: DistanceY(g1,g1) = 330.2
    c: PointOnObject(g2,g1)
    c: PointOnObject(g2,g0)
    c: Horizontal(g2)
    c: Coincident(g3,g1)
    c: Coincident(g3,g0)
    c: Coincident(g4,g2)
    c: Coincident(g4,g1)
    c: Coincident(g0,g4)
    c: Symmetric(g1,g1,g2)
FEATURE [PartDesign::Pad] Pad004
  BaseFeature = -> Pad003
  Direction = (1,0,0)
  Length = 25
  Length2 = 10
  Midplane = true
  Profile = -> Sketch009
  ReferenceAxis = -> Sketch009 [N_Axis]
  Refine = true
  Suppressed = false
  Type = 0
FEATURE [PartDesign::Fillet] Fillet001
  Base = -> Pad004 [Edge70,Edge67,Edge69,Edge68,Edge72,Edge71]
  BaseFeature = -> Pad004
  Radius = 5
  Refine = true
  SupportTransform = false
  Suppressed = false
  UseAllEdges = false
FEATURE [Sketcher::SketchObject] Sketch010
  ArcFitTolerance = 1e-06
  AttachmentSupport = -> [Fillet001]
  ExternalGeometry = -> [Fillet001]
  FullyConstrained = true
  MakeInternals = false
  MapMode = 5
  Placement = pos=(-12.5,0,0) rot=(0.57735,-0.57735,-0.57735;2.0944rad)
  sketch-geometry (6):
    g0: Circle CenterX=-187.334 CenterY=351.344 CenterZ=0 NormalX=0 NormalY=0 NormalZ=1 AngleXU=0 Radius=6
    g1: Circle CenterX=-199.784 CenterY=270.092 CenterZ=0 NormalX=0 NormalY=0 NormalZ=1 AngleXU=0 Radius=6
    g2: LineSegment [constr] StartX=-187.334 StartY=351.344 StartZ=0 EndX=-168.24 EndY=347.33 EndZ=0
    g3: LineSegment [constr] StartX=-199.784 StartY=270.092 StartZ=0 EndX=-180.133 EndY=268.289 EndZ=0
    g4: LineSegment [constr] StartX=-199.784 StartY=270.092 StartZ=0 EndX=-219.435 EndY=271.895 EndZ=0
    g5: LineSegment [constr] StartX=-187.334 StartY=351.344 StartZ=0 EndX=-206.427 EndY=355.357 EndZ=0
  constraints (18):
    c: Diameter(g0) = 12
    c: Distance(g0,g-3) = 20
    c: Diameter(g1) = 12
    c: Distance(g0,g1) = 76.2
    c: Coincident(g2,g0)
    c: PointOnObject(g2,g-5)
    c: Coincident(g4,g1)
    c: PointOnObject(g4,g-4)
    c: Coincident(g5,g0)
    c: PointOnObject(g5,g-4)
    c: Equal(g4,g3)
    c: Equal(g2,g5)
    c: Coincident(g3,g1)
    c: PointOnObject(g3,g-5)
    c: Parallel(g3,g4)
    c: Perpendicular(g-5,g3)
    c: Perpendicular(g-5,g2)
    c: Parallel(g2,g5)
FEATURE [PartDesign::Pocket] Pocket001
  BaseFeature = -> Fillet001
  Direction = (1,0,0)
  Length = 5
  Length2 = 5
  Profile = -> Sketch010
  ReferenceAxis = -> Sketch010 [N_Axis]
  Refine = true
  Suppressed = false
  Type = 1
FEATURE [PartDesign::Body] Body001  label="Stand"
  AllowCompound = false
  Group = -> [Sketch005,Pad001,Sketch006,Pad002,Sketch007,Pocket,Fillet,Sketch008,Pad003,Sketch009,Pad004,Fillet001,Sketch010,Pocket001]
  Origin = -> Origin001
  Tip = -> Pocket001
COMPONENT P7 — recipe-attached ("Vessel Holder001", modeled in this document).
Construction recipe (the document's own serialized feature program — sketch geometry with constraints, then the solid features built on it; lengths are millimeters unless a unit is written):

FEATURE [Sketcher::SketchObject] Sketch014
  ArcFitTolerance = 1e-06
  AttachmentSupport = -> [XY_Plane003]
  FullyConstrained = true
  MakeInternals = false
  MapMode = 5
  expr: Constraints[20] = VarSet.Plunger_Clearance_Length + 12.45 mm
  sketch-geometry (9):
    g0: LineSegment StartX=-85.78 StartY=-12.5 StartZ=0 EndX=-85.78 EndY=12.5 EndZ=0
    g1: LineSegment StartX=-85.78 StartY=12.5 StartZ=0 EndX=-115.78 EndY=12.5 EndZ=0
    g2: LineSegment StartX=-115.78 StartY=12.5 StartZ=0 EndX=-115.78 EndY=34.9255 EndZ=0
    g3: LineSegment StartX=-115.78 StartY=34.9255 StartZ=0 EndX=-35.78 EndY=34.9255 EndZ=0
    g4: LineSegment StartX=-35.78 StartY=-34.9255 StartZ=0 EndX=-115.78 EndY=-34.9255 EndZ=0
    g5: LineSegment StartX=-115.78 StartY=-34.9255 StartZ=0 EndX=-115.78 EndY=-12.5 EndZ=0
    g6: LineSegment StartX=-115.78 StartY=-12.5 StartZ=0 EndX=-85.78 EndY=-12.5 EndZ=0
    g7: ArcOfCircle CenterX=0 CenterY=1.8e-15 CenterZ=0 NormalX=0 NormalY=0 NormalZ=1 AngleXU=0 Radius=50 StartAngle=3.91491 EndAngle=8.65146
    g8: Circle CenterX=0 CenterY=1.8e-15 CenterZ=0 NormalX=0 NormalY=0 NormalZ=1 AngleXU=0 Radius=43.33
  constraints (26):
    c: Vertical(g0)
    c: Coincident(g0,g1)
    c: Horizontal(g1)
    c: Coincident(g1,g2)
    c: Vertical(g2)
    c: Coincident(g2,g3)
    c: Horizontal(g3)
    c: Horizontal(g4)
    c: Coincident(g4,g5)
    c: Vertical(g5)
    c: Coincident(g5,g6)
    c: Coincident(g6,g0)
    c: Horizontal(g6)
    c: Equal(g2,g5)
    c: Equal(g1,g6)
    c: Coincident(g7,g3)
    c: Coincident(g7,g4)
    c: Radius(g7) = 50
    c: Coincident(g8,g7)
    c: Diameter(g8) = 86.66
    c: Distance(g8,g0) = 42.45
    c: Symmetric(g3,g4,g-1)
    c: Coincident(g7,g-1)
    c: DistanceY(g0,g0) = 25
    c: DistanceX(g1,g1) = 30
    c: DistanceX(g3,g3) = 80
FEATURE [PartDesign::Pad] Pad006
  Direction = (0,0,1)
  Length = 30
  Length2 = 10
  Profile = -> Sketch014
  ReferenceAxis = -> Sketch014 [N_Axis]
  Refine = true
  Suppressed = false
  Type = 0
FEATURE [Sketcher::SketchObject] Sketch015
  ArcFitTolerance = 1e-06
  AttachmentSupport = -> [Pad006]
  ExternalGeometry = -> [Pad006]
  FullyConstrained = true
  MakeInternals = false
  MapMode = 5
  Placement = pos=(0,-34.9255,0) rot=(1,0,0;1.5708rad)
  sketch-geometry (3):
    g0: Circle CenterX=-100.78 CenterY=15 CenterZ=0 NormalX=0 NormalY=0 NormalZ=1 AngleXU=0 Radius=6
    g1: LineSegment [constr] StartX=-100.78 StartY=15 StartZ=0 EndX=-100.78 EndY=0 EndZ=0
    g2: LineSegment [constr] StartX=-100.78 StartY=15 StartZ=0 EndX=-100.78 EndY=30 EndZ=0
  constraints (9):
    c: Diameter(g0) = 12
    c: Distance(g0,g-4) = 15
    c: Coincident(g1,g0)
    c: PointOnObject(g1,g-5)
    c: Vertical(g1)
    c: Coincident(g2,g0)
    c: PointOnObject(g2,g-3)
    c: Vertical(g2)
    c: Equal(g2,g1)
FEATURE [PartDesign::Pocket] Pocket004
  BaseFeature = -> Pad006
  Direction = (0,1,-2e-16)
  Length = 5
  Length2 = 5
  Profile = -> Sketch015
  ReferenceAxis = -> Sketch015 [N_Axis]
  Refine = true
  Suppressed = false
  Type = 1
FEATURE [PartDesign::Body] Body003  label="Vessel Holder"
  AllowCompound = false
  Group = -> [Sketch014,Pad006,Sketch015,Pocket004]
  Origin = -> Origin003
  Tip = -> Pocket004
PROVENANCE & LICENSES
A FreeCAD (.FCStd) document from a public repository crawl; recipes are the document's own serialized feature recipes (and, for linked parts, companion documents' recipes).
License: as declared in the source repository (recorded in the dataset sidecar).
